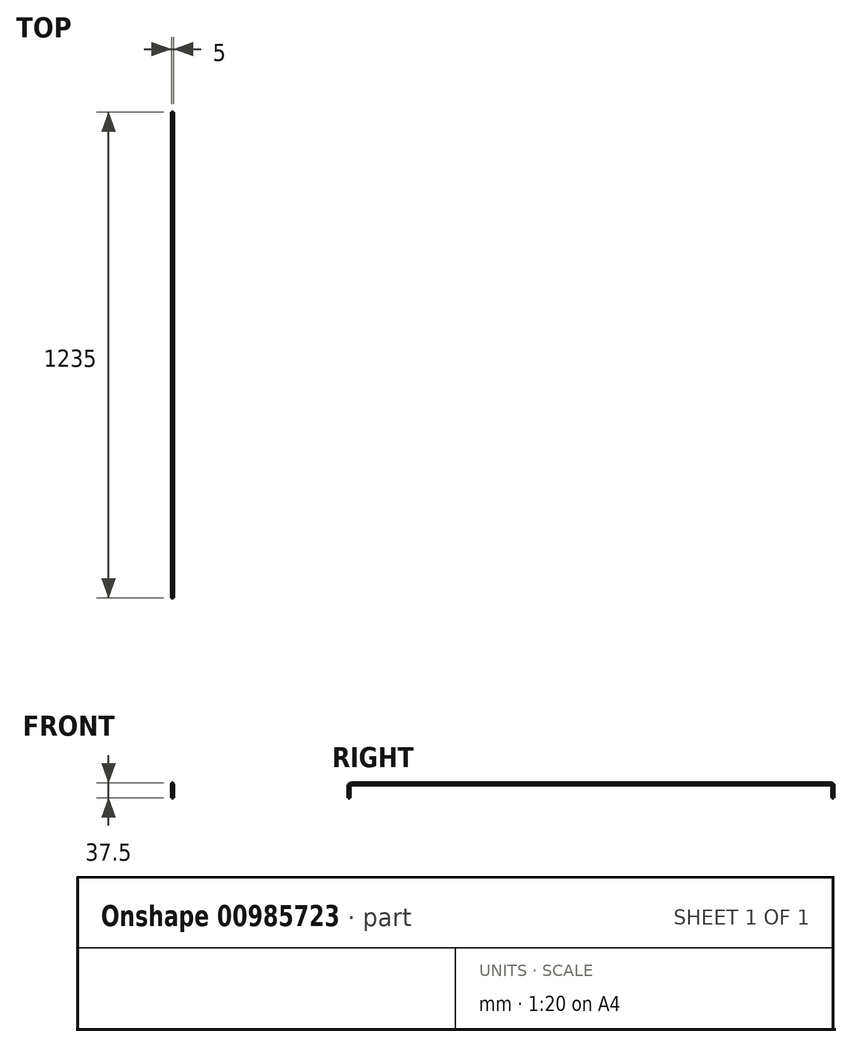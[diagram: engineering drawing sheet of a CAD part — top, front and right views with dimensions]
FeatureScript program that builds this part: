
annotation { "Feature Type Name" : "Feature", "Feature Type Description" : "" }
export const myFeature = defineFeature(function(context is Context, id is Id, definition is map)
    precondition{}
    {
        {
            var Q0;
            Q0=qCreatedBy(makeId("Right.planeOp"),FACE);
            var sketch = newSketch(context, id + "F0", { "sketchPlane" : qUnion([Q0])});
            skLineSegment(sketch, "E0", {"start": v(0, 0) * mm, "end": v(0, 30) * mm});
            skLineSegment(sketch, "E1", {"start": v(5, 35) * mm, "end": v(1225, 35) * mm});
            skLineSegment(sketch, "E2", {"start": v(1230, 30) * mm, "end": v(1230, 0) * mm});
            skPoint(sketch, "E3.visualSharp", {"position": v(0, 35) * mm});
            skArc(sketch, "E3.filletArc", {"start": v(5, 35) * mm, "mid": v(1.46, 33.54) * mm, "end": v(0, 30) * mm});
            skPoint(sketch, "E4.visualSharp", {"position": v(1230, 35) * mm});
            skArc(sketch, "E4.filletArc", {"start": v(1230, 30) * mm, "mid": v(1228.54, 33.54) * mm, "end": v(1225, 35) * mm});
            skSolve(sketch);
        }
        {
            var Q0;
            Q0=qCreatedBy(makeId("Top.planeOp"),FACE);
            var sketch = newSketch(context, id + "F1", { "sketchPlane" : qUnion([Q0])});
            skCircle(sketch, "E5", {"center": v(0, 0) * mm, "radius": 2.5 * mm});
            skSolve(sketch);
        }
        {
            var Q0;
            Q0=makeQuery(id+"F1.imprint","IMPRINT",FACE,{"disambiguationData":[TD([[makeQuery(id+"F1.imprint","IMPRINT",EDGE,{"derivedFrom":sQuery(id+"F1.wireOp",EDGE,"E5")}),1.0]])]});
            var Q1;
            Q1=sQuery(id+"F0.wireOp",EDGE,"E0");
            var Q2;
            Q2=sQuery(id+"F0.wireOp",EDGE,"E3.filletArc");
            var Q3;
            Q3=sQuery(id+"F0.wireOp",EDGE,"E1");
            var Q4;
            Q4=sQuery(id+"F0.wireOp",EDGE,"E4.filletArc");
            var Q5;
            Q5=sQuery(id+"F0.wireOp",EDGE,"E2");
            sweep(context, id + "F2", {"profiles" : qUnion([Q0]), "path" : qUnion([Q1, Q2, Q3, Q4, Q5])});
        }
    });
